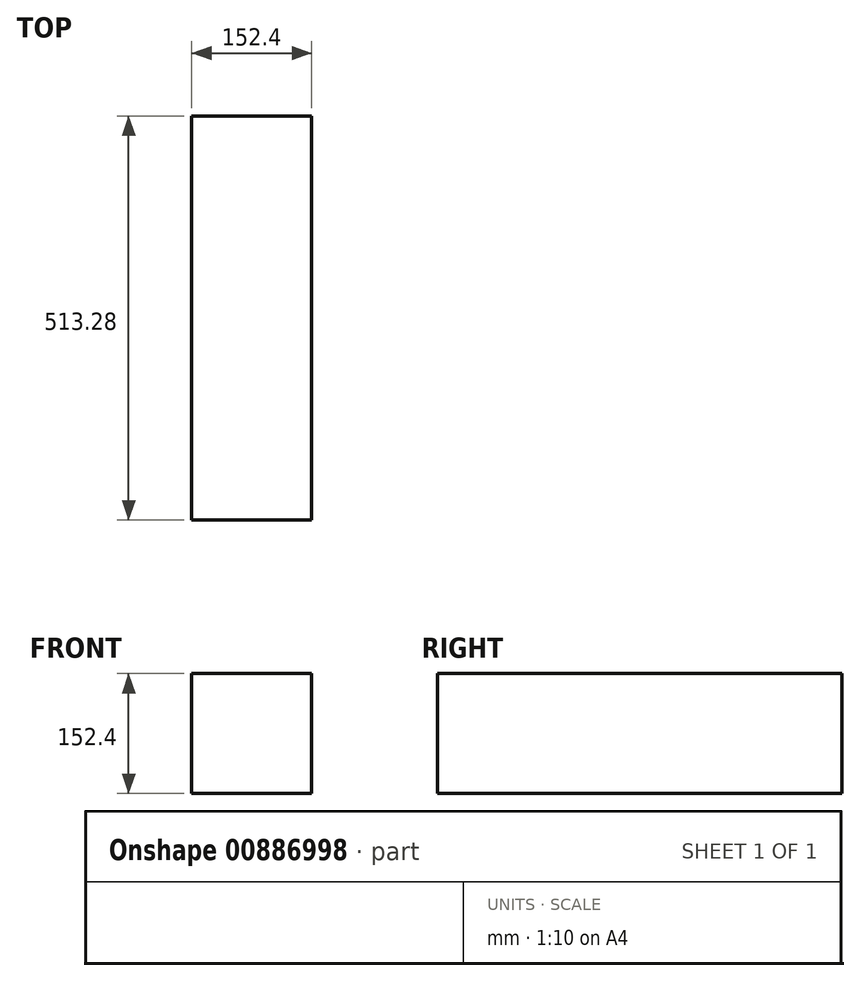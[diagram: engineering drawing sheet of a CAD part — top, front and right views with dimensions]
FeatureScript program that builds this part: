
annotation { "Feature Type Name" : "Feature", "Feature Type Description" : "" }
export const myFeature = defineFeature(function(context is Context, id is Id, definition is map)
    precondition{}
    {
        {
            var Q0;
            Q0=qCreatedBy(makeId("Front.planeOp"),FACE);
            var sketch = newSketch(context, id + "F0", { "sketchPlane" : qUnion([Q0])});
            skLineSegment(sketch, "E0.bottom", {"start": v(0, 0) * mm, "end": v(152.4, 0) * mm});
            skLineSegment(sketch, "E0.top", {"start": v(0, 152.4) * mm, "end": v(152.4, 152.4) * mm});
            skLineSegment(sketch, "E0.left", {"start": v(0, 0) * mm, "end": v(0, 152.4) * mm});
            skLineSegment(sketch, "E0.right", {"start": v(152.4, 0) * mm, "end": v(152.4, 152.4) * mm});
            skSolve(sketch);
        }
        {
            var Q0;
            Q0 = qSketchRegion(id + "F0", true);
            extrude(context, id + "F1", {"entities" : qUnion([Q0]), "depth" : 513.28 * mm, "offsetDistance" : 25.4 * mm});
        }
    });
